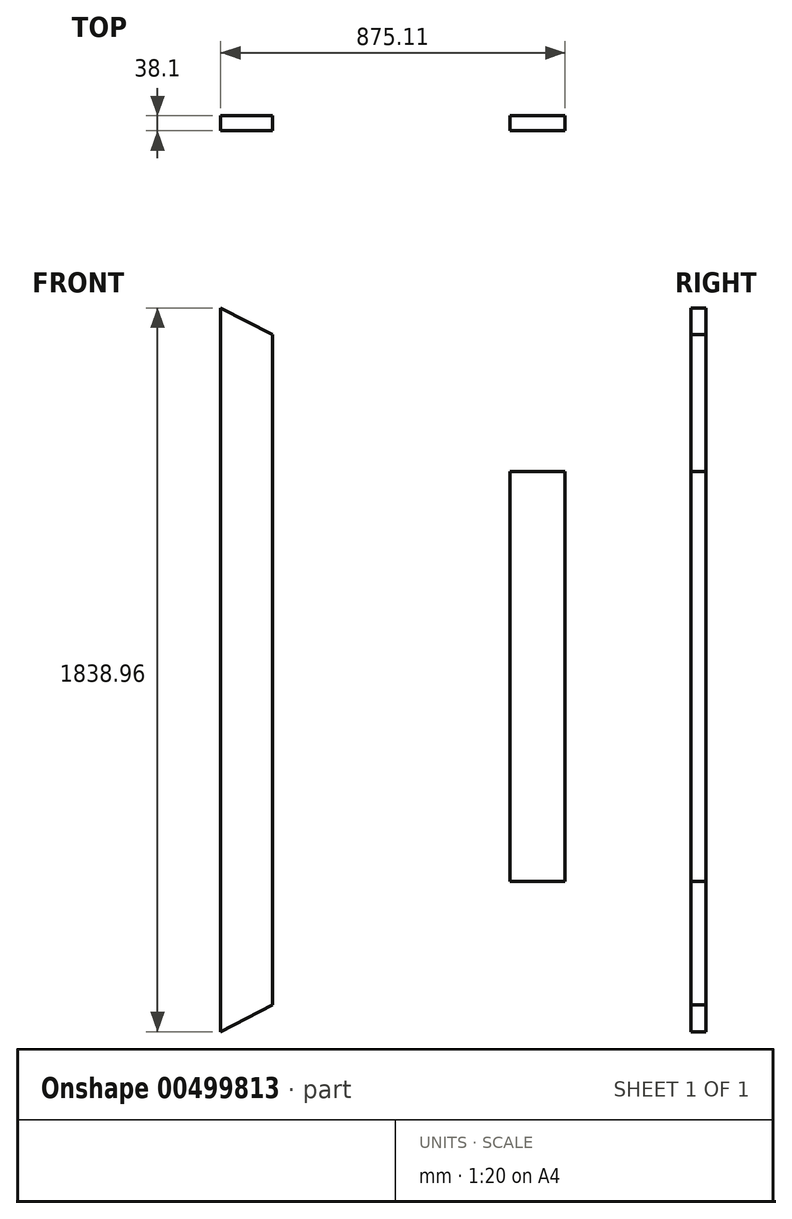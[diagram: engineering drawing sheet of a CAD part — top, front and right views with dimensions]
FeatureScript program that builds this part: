
annotation { "Feature Type Name" : "Feature", "Feature Type Description" : "" }
export const myFeature = defineFeature(function(context is Context, id is Id, definition is map)
    precondition{}
    {
        {
            var Q0;
            Q0=qCreatedBy(makeId("Front.planeOp"),FACE);
            var sketch = newSketch(context, id + "F0", { "sketchPlane" : qUnion([Q0])});
            skLineSegment(sketch, "E0.left", {"start": v(57.99, -835.34) * mm, "end": v(57.99, 868.63) * mm});
            skLineSegment(sketch, "E0.right", {"start": v(-74.47, -902.83) * mm, "end": v(-74.47, 936.13) * mm});
            skPoint(sketch, "E0.middle", {"position": v(-11.86, 0) * mm});
            skLineSegment(sketch, "E1", {"start": v(-74.47, 936.13) * mm, "end": v(57.99, 868.63) * mm});
            skLineSegment(sketch, "E2", {"start": v(-74.47, -902.83) * mm, "end": v(57.99, -835.34) * mm});
            skSolve(sketch);
        }
        {
            var Q0;
            Q0 = qSketchRegion(id + "F0", true);
            extrude(context, id + "F1", {"entities" : qUnion([Q0]), "depth" : 38.1 * mm});
        }
        {
            var Q0;
            Q0=qCreatedBy(makeId("Front.planeOp"),FACE);
            var sketch = newSketch(context, id + "F2", { "sketchPlane" : qUnion([Q0])});
            skLineSegment(sketch, "E3.bottom", {"start": v(800.64, -520.7) * mm, "end": v(660.94, -520.7) * mm});
            skLineSegment(sketch, "E3.top", {"start": v(800.64, 520.7) * mm, "end": v(660.94, 520.7) * mm});
            skLineSegment(sketch, "E3.left", {"start": v(800.64, -520.7) * mm, "end": v(800.64, 520.7) * mm});
            skLineSegment(sketch, "E3.right", {"start": v(660.94, -520.7) * mm, "end": v(660.94, 520.7) * mm});
            skPoint(sketch, "E3.middle", {"position": v(730.8, 0) * mm});
            skSolve(sketch);
        }
        {
            var Q0;
            Q0 = qSketchRegion(id + "F2", true);
            extrude(context, id + "F3", {"entities" : qUnion([Q0]), "depth" : 38.1 * mm});
        }
    });
